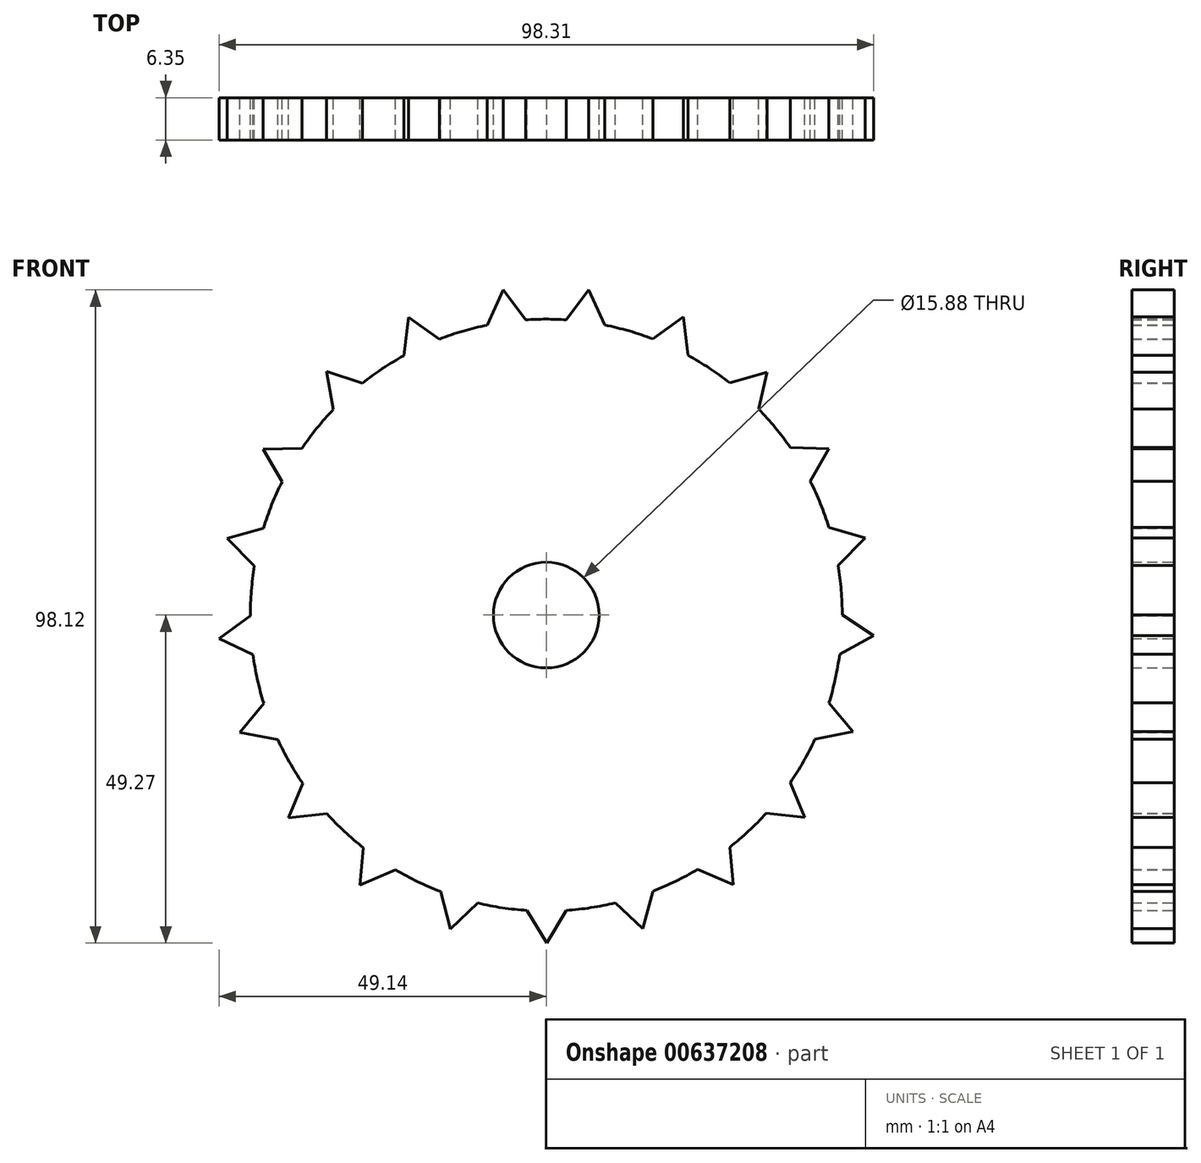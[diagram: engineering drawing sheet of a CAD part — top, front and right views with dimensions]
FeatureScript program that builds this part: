
annotation { "Feature Type Name" : "Feature", "Feature Type Description" : "" }
export const myFeature = defineFeature(function(context is Context, id is Id, definition is map)
    precondition{}
    {
        {
            var Q0;
            Q0=qCreatedBy(makeId("Front.planeOp"),FACE);
            var sketch = newSketch(context, id + "F0", { "sketchPlane" : qUnion([Q0])});
            skCircle(sketch, "E0", {"center": v(0, 0) * mm, "radius": 7.94 * mm});
            skCircle(sketch, "E1", {"center": v(0, 0) * mm, "radius": 44.45 * mm});
            skLineSegment(sketch, "E2", {"start": v(2.98, 44.35) * mm, "end": v(5.9, 44.06) * mm, "construction": true});
            skLineSegment(sketch, "E3", {"start": v(5.9, 44.06) * mm, "end": v(8.79, 43.57) * mm});
            skLineSegment(sketch, "E4", {"start": v(5.9, 44.06) * mm, "end": v(6.38, 48.85) * mm, "construction": true});
            skLineSegment(sketch, "E5", {"start": v(6.38, 48.85) * mm, "end": v(2.98, 44.35) * mm});
            skLineSegment(sketch, "E6", {"start": v(6.38, 48.85) * mm, "end": v(8.79, 43.57) * mm});
            skLineSegment(sketch, "E7", {"start": v(8.79, 43.57) * mm, "end": v(15.98, 41.48) * mm, "construction": true});
            skLineSegment(sketch, "E8", {"start": v(15.98, 41.48) * mm, "end": v(18.68, 40.33) * mm});
            skLineSegment(sketch, "E9", {"start": v(18.68, 40.33) * mm, "end": v(20.56, 44.77) * mm, "construction": true});
            skLineSegment(sketch, "E10", {"start": v(18.68, 40.33) * mm, "end": v(21.3, 39.01) * mm, "construction": true});
            skLineSegment(sketch, "E11", {"start": v(15.98, 41.48) * mm, "end": v(20.56, 44.77) * mm});
            skLineSegment(sketch, "E12", {"start": v(21.3, 39.01) * mm, "end": v(20.56, 44.77) * mm});
            skLineSegment(sketch, "E13", {"start": v(21.3, 39.01) * mm, "end": v(27.55, 34.88) * mm, "construction": true});
            skLineSegment(sketch, "E14", {"start": v(27.55, 34.88) * mm, "end": v(29.8, 32.99) * mm, "construction": true});
            skLineSegment(sketch, "E15", {"start": v(29.8, 32.99) * mm, "end": v(31.9, 30.95) * mm, "construction": true});
            skLineSegment(sketch, "E16", {"start": v(29.8, 32.99) * mm, "end": v(33.14, 36.46) * mm, "construction": true});
            skLineSegment(sketch, "E17", {"start": v(27.55, 34.88) * mm, "end": v(33.14, 36.46) * mm});
            skLineSegment(sketch, "E18", {"start": v(33.14, 36.46) * mm, "end": v(31.9, 30.95) * mm});
            skLineSegment(sketch, "E19", {"start": v(31.9, 30.95) * mm, "end": v(36.65, 25.15) * mm, "construction": true});
            skLineSegment(sketch, "E20", {"start": v(36.65, 25.15) * mm, "end": v(38.23, 22.68) * mm, "construction": true});
            skLineSegment(sketch, "E21", {"start": v(38.23, 22.68) * mm, "end": v(39.64, 20.12) * mm, "construction": true});
            skLineSegment(sketch, "E22", {"start": v(38.23, 22.68) * mm, "end": v(42.45, 25) * mm, "construction": true});
            skLineSegment(sketch, "E23", {"start": v(36.65, 25.15) * mm, "end": v(42.45, 25) * mm});
            skLineSegment(sketch, "E24", {"start": v(42.45, 25) * mm, "end": v(39.64, 20.12) * mm});
            skLineSegment(sketch, "E25", {"start": v(39.64, 20.12) * mm, "end": v(42.45, 13.17) * mm, "construction": true});
            skLineSegment(sketch, "E26", {"start": v(42.45, 13.17) * mm, "end": v(43.23, 10.34) * mm, "construction": true});
            skLineSegment(sketch, "E27", {"start": v(43.23, 10.34) * mm, "end": v(43.82, 7.47) * mm, "construction": true});
            skLineSegment(sketch, "E28", {"start": v(43.23, 10.34) * mm, "end": v(47.88, 11.62) * mm, "construction": true});
            skLineSegment(sketch, "E29", {"start": v(42.45, 13.17) * mm, "end": v(47.88, 11.62) * mm});
            skLineSegment(sketch, "E30", {"start": v(47.88, 11.62) * mm, "end": v(43.82, 7.47) * mm});
            skLineSegment(sketch, "E31", {"start": v(43.82, 7.47) * mm, "end": v(44.45, 0) * mm, "construction": true});
            skLineSegment(sketch, "E32", {"start": v(44.45, 0) * mm, "end": v(44.35, -2.93) * mm, "construction": true});
            skLineSegment(sketch, "E33", {"start": v(44.35, -2.93) * mm, "end": v(44.06, -5.84) * mm, "construction": true});
            skLineSegment(sketch, "E34", {"start": v(44.35, -2.93) * mm, "end": v(49.17, -3.09) * mm, "construction": true});
            skLineSegment(sketch, "E35", {"start": v(44.45, 0) * mm, "end": v(49.17, -3.09) * mm});
            skLineSegment(sketch, "E36", {"start": v(49.17, -3.09) * mm, "end": v(44.06, -5.84) * mm});
            skLineSegment(sketch, "E37", {"start": v(44.06, -5.84) * mm, "end": v(42.45, -13.17) * mm, "construction": true});
            skLineSegment(sketch, "E38", {"start": v(42.45, -13.17) * mm, "end": v(41.5, -15.94) * mm});
            skLineSegment(sketch, "E39", {"start": v(41.5, -15.94) * mm, "end": v(40.35, -18.64) * mm, "construction": true});
            skLineSegment(sketch, "E40", {"start": v(41.5, -15.94) * mm, "end": v(46.05, -17.52) * mm, "construction": true});
            skLineSegment(sketch, "E41", {"start": v(42.45, -13.17) * mm, "end": v(46.05, -17.52) * mm});
            skLineSegment(sketch, "E42", {"start": v(46.05, -17.52) * mm, "end": v(40.35, -18.64) * mm});
            skLineSegment(sketch, "E43", {"start": v(40.35, -18.64) * mm, "end": v(36.65, -25.15) * mm, "construction": true});
            skLineSegment(sketch, "E44", {"start": v(36.65, -25.15) * mm, "end": v(34.91, -27.51) * mm, "construction": true});
            skLineSegment(sketch, "E45", {"start": v(34.91, -27.51) * mm, "end": v(33.02, -29.75) * mm, "construction": true});
            skLineSegment(sketch, "E46", {"start": v(34.91, -27.51) * mm, "end": v(38.8, -30.37) * mm, "construction": true});
            skLineSegment(sketch, "E47", {"start": v(33.02, -29.75) * mm, "end": v(27.55, -34.88) * mm, "construction": true});
            skLineSegment(sketch, "E48", {"start": v(36.65, -25.15) * mm, "end": v(38.8, -30.37) * mm});
            skLineSegment(sketch, "E49", {"start": v(38.8, -30.37) * mm, "end": v(33.02, -29.75) * mm});
            skLineSegment(sketch, "E50", {"start": v(27.55, -34.88) * mm, "end": v(25.2, -36.62) * mm, "construction": true});
            skLineSegment(sketch, "E51", {"start": v(25.2, -36.62) * mm, "end": v(22.73, -38.2) * mm, "construction": true});
            skLineSegment(sketch, "E52", {"start": v(25.2, -36.62) * mm, "end": v(28.06, -40.5) * mm, "construction": true});
            skLineSegment(sketch, "E53", {"start": v(27.55, -34.88) * mm, "end": v(28.06, -40.5) * mm});
            skLineSegment(sketch, "E54", {"start": v(28.06, -40.5) * mm, "end": v(22.73, -38.2) * mm});
            skLineSegment(sketch, "E55", {"start": v(22.73, -38.2) * mm, "end": v(15.98, -41.48) * mm, "construction": true});
            skLineSegment(sketch, "E56", {"start": v(15.98, -41.48) * mm, "end": v(13.22, -42.44) * mm, "construction": true});
            skLineSegment(sketch, "E57", {"start": v(13.22, -42.44) * mm, "end": v(10.4, -43.22) * mm, "construction": true});
            skLineSegment(sketch, "E58", {"start": v(13.22, -42.44) * mm, "end": v(14.5, -47.09) * mm, "construction": true});
            skLineSegment(sketch, "E59", {"start": v(10.4, -43.22) * mm, "end": v(14.5, -47.09) * mm});
            skLineSegment(sketch, "E60", {"start": v(14.5, -47.09) * mm, "end": v(15.98, -41.48) * mm});
            skLineSegment(sketch, "E61", {"start": v(10.4, -43.22) * mm, "end": v(2.98, -44.35) * mm, "construction": true});
            skLineSegment(sketch, "E62", {"start": v(2.98, -44.35) * mm, "end": v(0.05, -44.45) * mm, "construction": true});
            skLineSegment(sketch, "E63", {"start": v(0.05, -44.45) * mm, "end": v(-2.88, -44.36) * mm, "construction": true});
            skLineSegment(sketch, "E64", {"start": v(0.05, -44.45) * mm, "end": v(0.05, -49.27) * mm, "construction": true});
            skLineSegment(sketch, "E65", {"start": v(2.98, -44.35) * mm, "end": v(0.05, -49.27) * mm});
            skLineSegment(sketch, "E66", {"start": v(-2.88, -44.36) * mm, "end": v(0.05, -49.27) * mm});
            skLineSegment(sketch, "E67", {"start": v(-2.88, -44.36) * mm, "end": v(-10.3, -43.24) * mm, "construction": true});
            skLineSegment(sketch, "E68", {"start": v(-10.3, -43.24) * mm, "end": v(-13.12, -42.47) * mm, "construction": true});
            skLineSegment(sketch, "E69", {"start": v(-13.12, -42.47) * mm, "end": v(-15.89, -41.51) * mm, "construction": true});
            skLineSegment(sketch, "E70", {"start": v(-13.12, -42.47) * mm, "end": v(-14.39, -47.12) * mm, "construction": true});
            skLineSegment(sketch, "E71", {"start": v(-15.89, -41.51) * mm, "end": v(-14.39, -47.12) * mm});
            skLineSegment(sketch, "E72", {"start": v(-14.39, -47.12) * mm, "end": v(-10.3, -43.24) * mm});
            skLineSegment(sketch, "E73", {"start": v(-15.89, -41.51) * mm, "end": v(-22.64, -38.25) * mm, "construction": true});
            skLineSegment(sketch, "E74", {"start": v(-22.64, -38.25) * mm, "end": v(-25.11, -36.68) * mm, "construction": true});
            skLineSegment(sketch, "E75", {"start": v(-25.11, -36.68) * mm, "end": v(-27.47, -34.94) * mm, "construction": true});
            skLineSegment(sketch, "E76", {"start": v(-25.11, -36.68) * mm, "end": v(-27.96, -40.56) * mm, "construction": true});
            skLineSegment(sketch, "E77", {"start": v(-27.47, -34.94) * mm, "end": v(-27.96, -40.56) * mm});
            skLineSegment(sketch, "E78", {"start": v(-22.64, -38.25) * mm, "end": v(-27.96, -40.56) * mm});
            skLineSegment(sketch, "E79", {"start": v(-27.47, -34.94) * mm, "end": v(-32.95, -29.83) * mm, "construction": true});
            skLineSegment(sketch, "E80", {"start": v(-32.95, -29.83) * mm, "end": v(-34.85, -27.6) * mm, "construction": true});
            skLineSegment(sketch, "E81", {"start": v(-34.85, -27.6) * mm, "end": v(-36.6, -25.24) * mm, "construction": true});
            skLineSegment(sketch, "E82", {"start": v(-34.85, -27.6) * mm, "end": v(-38.73, -30.46) * mm, "construction": true});
            skLineSegment(sketch, "E83", {"start": v(-36.6, -25.24) * mm, "end": v(-38.73, -30.46) * mm});
            skLineSegment(sketch, "E84", {"start": v(-32.95, -29.83) * mm, "end": v(-38.73, -30.46) * mm});
            skLineSegment(sketch, "E85", {"start": v(-36.6, -25.24) * mm, "end": v(-40.31, -18.73) * mm, "construction": true});
            skLineSegment(sketch, "E86", {"start": v(-40.31, -18.73) * mm, "end": v(-41.46, -16.03) * mm, "construction": true});
            skLineSegment(sketch, "E87", {"start": v(-41.46, -16.03) * mm, "end": v(-42.42, -13.27) * mm, "construction": true});
            skLineSegment(sketch, "E88", {"start": v(-41.46, -16.03) * mm, "end": v(-46.01, -17.62) * mm, "construction": true});
            skLineSegment(sketch, "E89", {"start": v(-40.31, -18.73) * mm, "end": v(-46.01, -17.62) * mm});
            skLineSegment(sketch, "E90", {"start": v(-42.42, -13.27) * mm, "end": v(-46.01, -17.62) * mm});
            skLineSegment(sketch, "E91", {"start": v(-42.42, -13.27) * mm, "end": v(-44.05, -5.95) * mm, "construction": true});
            skLineSegment(sketch, "E92", {"start": v(-44.05, -5.95) * mm, "end": v(-44.35, -3.03) * mm, "construction": true});
            skLineSegment(sketch, "E93", {"start": v(-44.35, -3.03) * mm, "end": v(-44.45, -0.1) * mm, "construction": true});
            skLineSegment(sketch, "E94", {"start": v(-44.35, -3.03) * mm, "end": v(-49.14, -3.52) * mm, "construction": true});
            skLineSegment(sketch, "E95", {"start": v(-49.14, -3.52) * mm, "end": v(-44.05, -5.95) * mm});
            skLineSegment(sketch, "E96", {"start": v(-49.14, -3.52) * mm, "end": v(-44.45, -0.1) * mm});
            skLineSegment(sketch, "E97", {"start": v(-44.45, -0.1) * mm, "end": v(-43.83, 7.37) * mm, "construction": true});
            skLineSegment(sketch, "E98", {"start": v(-43.83, 7.37) * mm, "end": v(-43.25, 10.24) * mm, "construction": true});
            skLineSegment(sketch, "E99", {"start": v(-43.25, 10.24) * mm, "end": v(-42.49, 13.07) * mm, "construction": true});
            skLineSegment(sketch, "E100", {"start": v(-43.25, 10.24) * mm, "end": v(-47.9, 11.5) * mm, "construction": true});
            skLineSegment(sketch, "E101", {"start": v(-47.9, 11.5) * mm, "end": v(-43.83, 7.37) * mm});
            skLineSegment(sketch, "E102", {"start": v(-47.9, 11.5) * mm, "end": v(-42.49, 13.07) * mm});
            skLineSegment(sketch, "E103", {"start": v(-42.49, 13.07) * mm, "end": v(-39.68, 20.02) * mm, "construction": true});
            skLineSegment(sketch, "E104", {"start": v(-39.68, 20.02) * mm, "end": v(-38.28, 22.6) * mm, "construction": true});
            skLineSegment(sketch, "E105", {"start": v(-38.28, 22.6) * mm, "end": v(-36.7, 25.07) * mm, "construction": true});
            skLineSegment(sketch, "E106", {"start": v(-38.28, 22.6) * mm, "end": v(-42.5, 24.9) * mm, "construction": true});
            skLineSegment(sketch, "E107", {"start": v(-42.5, 24.9) * mm, "end": v(-39.68, 20.02) * mm});
            skLineSegment(sketch, "E108", {"start": v(-42.5, 24.9) * mm, "end": v(-36.7, 25.07) * mm});
            skLineSegment(sketch, "E109", {"start": v(-36.7, 25.07) * mm, "end": v(-31.97, 30.88) * mm, "construction": true});
            skLineSegment(sketch, "E110", {"start": v(-31.97, 30.88) * mm, "end": v(-29.87, 32.92) * mm, "construction": true});
            skLineSegment(sketch, "E111", {"start": v(-29.87, 32.92) * mm, "end": v(-27.63, 34.82) * mm, "construction": true});
            skLineSegment(sketch, "E112", {"start": v(-29.87, 32.92) * mm, "end": v(-32.99, 36.6) * mm, "construction": true});
            skLineSegment(sketch, "E113", {"start": v(-31.97, 30.88) * mm, "end": v(-32.99, 36.6) * mm});
            skLineSegment(sketch, "E114", {"start": v(-32.99, 36.6) * mm, "end": v(-27.63, 34.82) * mm});
            skLineSegment(sketch, "E115", {"start": v(-27.63, 34.82) * mm, "end": v(-21.39, 38.97) * mm, "construction": true});
            skLineSegment(sketch, "E116", {"start": v(-21.39, 38.97) * mm, "end": v(-18.77, 40.3) * mm, "construction": true});
            skLineSegment(sketch, "E117", {"start": v(-18.77, 40.3) * mm, "end": v(-16.08, 41.44) * mm, "construction": true});
            skLineSegment(sketch, "E118", {"start": v(-18.77, 40.3) * mm, "end": v(-20.67, 44.73) * mm, "construction": true});
            skLineSegment(sketch, "E119", {"start": v(-20.67, 44.73) * mm, "end": v(-21.39, 38.97) * mm});
            skLineSegment(sketch, "E120", {"start": v(-20.67, 44.73) * mm, "end": v(-16.08, 41.44) * mm});
            skLineSegment(sketch, "E121", {"start": v(-16.08, 41.44) * mm, "end": v(-8.89, 43.55) * mm, "construction": true});
            skLineSegment(sketch, "E122", {"start": v(-8.89, 43.55) * mm, "end": v(-6, 44.04) * mm, "construction": true});
            skLineSegment(sketch, "E123", {"start": v(-6, 44.04) * mm, "end": v(-3.08, 44.34) * mm, "construction": true});
            skLineSegment(sketch, "E124", {"start": v(-6, 44.04) * mm, "end": v(-6.49, 48.84) * mm, "construction": true});
            skLineSegment(sketch, "E125", {"start": v(-8.89, 43.55) * mm, "end": v(-6.49, 48.84) * mm});
            skLineSegment(sketch, "E126", {"start": v(-6.49, 48.84) * mm, "end": v(-3.08, 44.34) * mm});
            skLineSegment(sketch, "E127", {"start": v(-3.08, 44.34) * mm, "end": v(2.98, 44.35) * mm, "construction": true});
            skSolve(sketch);
        }
        {
            var Q0;
            Q0 = qSketchRegion(id + "F0", true);
            extrude(context, id + "F1", {"entities" : qUnion([Q0]), "depth" : 6.35 * mm, "offsetDistance" : 25.4 * mm});
        }
    });
